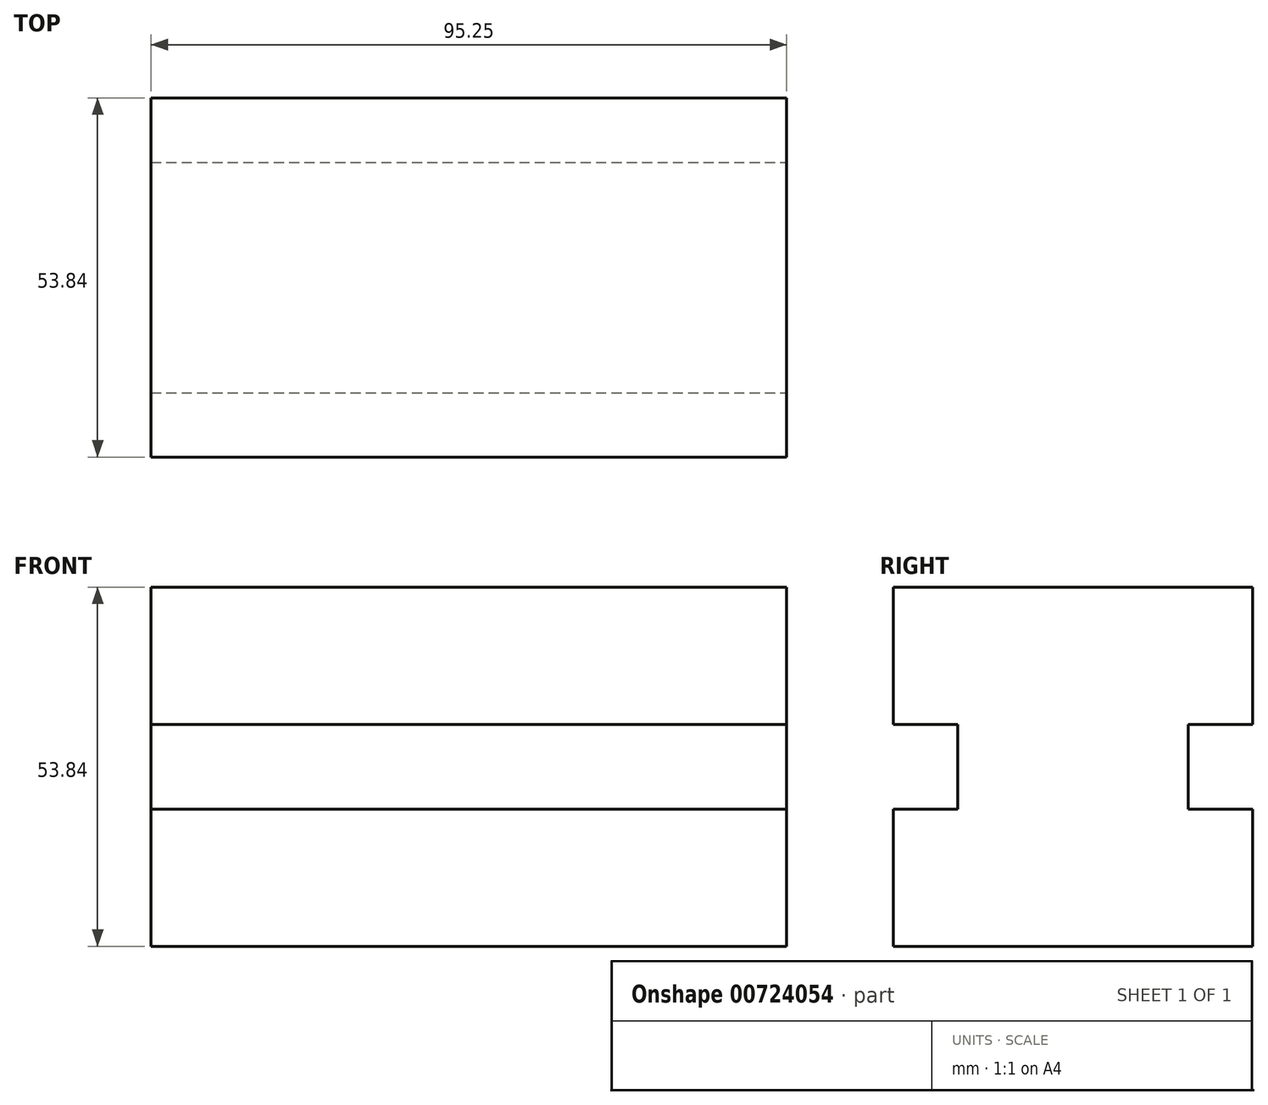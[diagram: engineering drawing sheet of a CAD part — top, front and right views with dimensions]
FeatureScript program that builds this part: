
annotation { "Feature Type Name" : "Feature", "Feature Type Description" : "" }
export const myFeature = defineFeature(function(context is Context, id is Id, definition is map)
    precondition{}
    {
        {
            var Q0;
            Q0=qCreatedBy(makeId("Right.planeOp"),FACE);
            var sketch = newSketch(context, id + "F0", { "sketchPlane" : qUnion([Q0])});
            skLineSegment(sketch, "E0.bottom", {"start": v(26.92, -26.92) * mm, "end": v(-26.92, -26.92) * mm});
            skLineSegment(sketch, "E0.top", {"start": v(26.92, 26.92) * mm, "end": v(-26.92, 26.92) * mm});
            skLineSegment(sketch, "E0.left", {"start": v(26.92, -26.92) * mm, "end": v(26.92, -6.35) * mm});
            skLineSegment(sketch, "E0.right", {"start": v(-26.92, -26.92) * mm, "end": v(-26.92, -6.35) * mm});
            skPoint(sketch, "E0.middle", {"position": v(0, 0) * mm});
            skLineSegment(sketch, "E1.bottom", {"start": v(-26.92, 6.35) * mm, "end": v(-17.27, 6.35) * mm});
            skLineSegment(sketch, "E1.top", {"start": v(-26.92, -6.35) * mm, "end": v(-17.27, -6.35) * mm});
            skLineSegment(sketch, "E1.right", {"start": v(-17.27, 6.35) * mm, "end": v(-17.27, -6.35) * mm});
            skLineSegment(sketch, "E2.trimOffspring", {"start": v(-26.92, 6.35) * mm, "end": v(-26.92, 26.92) * mm});
            skLineSegment(sketch, "E3", {"start": v(0, 30.08) * mm, "end": v(0, -29.47) * mm, "construction": true});
            skLineSegment(sketch, "E4.MirrorCS", {"start": v(26.92, 6.35) * mm, "end": v(17.27, 6.35) * mm});
            skLineSegment(sketch, "E5.MirrorCS", {"start": v(17.27, 6.35) * mm, "end": v(17.27, -6.35) * mm});
            skLineSegment(sketch, "E6.MirrorCS", {"start": v(26.92, -6.35) * mm, "end": v(17.27, -6.35) * mm});
            skLineSegment(sketch, "E7.trimOffspring", {"start": v(26.92, 6.35) * mm, "end": v(26.92, 26.92) * mm});
            skSolve(sketch);
        }
        {
            var Q0;
            Q0=makeQuery(id+"F0.imprint","IMPRINT",FACE,{"disambiguationData":[TD([[makeQuery(id+"F0.imprint","IMPRINT",EDGE,{"derivedFrom":sQuery(id+"F0.wireOp",EDGE,"E0.bottom")}),-1.0]])]});
            extrude(context, id + "F1", {"entities" : qUnion([Q0]), "oppositeDirection" : true, "depth" : 95.25 * mm, "offsetDistance" : 25.4 * mm});
        }
    });
